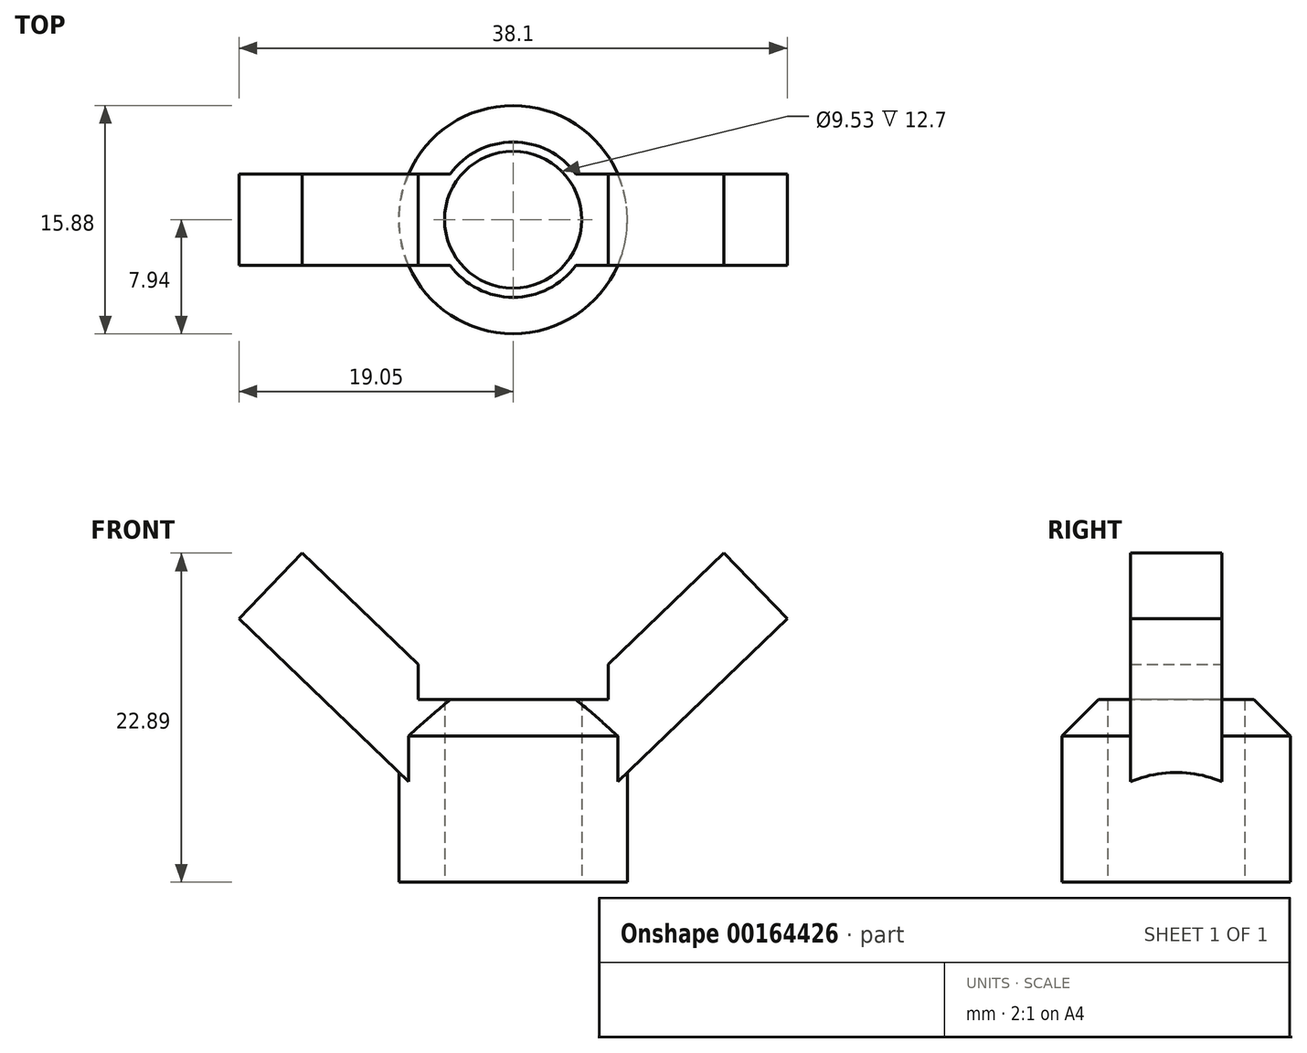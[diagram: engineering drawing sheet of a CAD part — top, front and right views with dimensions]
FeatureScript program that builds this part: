
annotation { "Feature Type Name" : "Feature", "Feature Type Description" : "" }
export const myFeature = defineFeature(function(context is Context, id is Id, definition is map)
    precondition{}
    {
        {
            var Q0;
            Q0=qCreatedBy(makeId("Front.planeOp"),FACE);
            var sketch = newSketch(context, id + "F0", { "sketchPlane" : qUnion([Q0])});
            skLineSegment(sketch, "E0", {"start": v(-6.6, 6.35) * mm, "end": v(-19.05, 18.32) * mm});
            skLineSegment(sketch, "E1", {"start": v(-19.05, 18.32) * mm, "end": v(-14.65, 22.9) * mm});
            skLineSegment(sketch, "E2", {"start": v(-14.65, 22.9) * mm, "end": v(-6.6, 15.16) * mm});
            skLineSegment(sketch, "E3", {"start": v(0, 0) * mm, "end": v(0, 75.67) * mm, "construction": true});
            skLineSegment(sketch, "E4", {"start": v(-6.6, 15.16) * mm, "end": v(-6.6, 6.35) * mm});
            skLineSegment(sketch, "E5", {"start": v(-6.6, 6.35) * mm, "end": v(-6.6, 0) * mm, "construction": true});
            skLineSegment(sketch, "E6", {"start": v(-6.6, 0) * mm, "end": v(0, 0) * mm, "construction": true});
            skLineSegment(sketch, "E7.MirrorCS", {"start": v(6.6, 6.35) * mm, "end": v(6.6, 0) * mm, "construction": true});
            skLineSegment(sketch, "E8.MirrorCS", {"start": v(6.6, 6.35) * mm, "end": v(19.05, 18.32) * mm});
            skLineSegment(sketch, "E9.MirrorCS", {"start": v(6.6, 15.16) * mm, "end": v(6.6, 6.35) * mm});
            skLineSegment(sketch, "E10.MirrorCS", {"start": v(14.65, 22.9) * mm, "end": v(6.6, 15.16) * mm});
            skLineSegment(sketch, "E11.MirrorCS", {"start": v(19.05, 18.32) * mm, "end": v(14.65, 22.9) * mm});
            skLineSegment(sketch, "E12.MirrorCS", {"start": v(6.6, 0) * mm, "end": v(0, 0) * mm, "construction": true});
            skSolve(sketch);
        }
        {
            var Q0;
            Q0=makeQuery(id+"F0.imprint","IMPRINT",FACE,{"disambiguationData":[TD([[makeQuery(id+"F0.imprint","IMPRINT",EDGE,{"derivedFrom":sQuery(id+"F0.wireOp",EDGE,"E0")}),-1.0]])]});
            var Q1;
            Q1=makeQuery(id+"F0.imprint","IMPRINT",FACE,{"disambiguationData":[TD([[makeQuery(id+"F0.imprint","IMPRINT",EDGE,{"derivedFrom":sQuery(id+"F0.wireOp",EDGE,"E8.MirrorCS")}),1.0]])]});
            extrude(context, id + "F1", {"entities" : qUnion([Q0, Q1]), "depth" : 3.17 * mm, "hasSecondDirection" : true, "secondDirectionOppositeDirection" : true, "secondDirectionDepth" : 3.17 * mm});
        }
        {
            var Q0;
            Q0=qCreatedBy(makeId("Top.planeOp"),FACE);
            var sketch = newSketch(context, id + "F2", { "sketchPlane" : qUnion([Q0])});
            skCircle(sketch, "E13", {"center": v(0, 0) * mm, "radius": 7.94 * mm});
            skCircle(sketch, "E14", {"center": v(0, 0) * mm, "radius": 4.76 * mm});
            skSolve(sketch);
        }
        {
            var Q0;
            Q0 = qSketchRegion(id + "F2", true);
            extrude(context, id + "F3", {"entities" : qUnion([Q0]), "operationType" : NewBodyOperationType.ADD, "depth" : 12.7 * mm});
        }
        {
            var Q0;
            {var subQ0=sQuery(id+"F2.wireOp",EDGE,"E13");Q0=makeQuery(id+"F3.boolean.opBoolean","SPLIT",EDGE,{"disambiguationData":[TD([makeQuery(id+"F1.opExtrude","CAP_FACE",FACE,{"disambiguationData":[OSD([sQuery(id+"F0.wireOp",EDGE,"E0"),sQuery(id+"F0.wireOp",EDGE,"E1"),sQuery(id+"F0.wireOp",EDGE,"E2"),sQuery(id+"F0.wireOp",EDGE,"E4")])],"isStart":false})])],"derivedFrom":makeQuery(id+"F3.opExtrude","CAP_EDGE",EDGE,{"disambiguationData":[OSD([subQ0])],"isStart":false})});}
            var Q1;
            {var subQ0=sQuery(id+"F2.wireOp",EDGE,"E13");Q1=makeQuery(id+"F3.boolean.opBoolean","SPLIT",EDGE,{"disambiguationData":[TD([makeQuery(id+"F1.opExtrude","CAP_FACE",FACE,{"disambiguationData":[OSD([sQuery(id+"F0.wireOp",EDGE,"E0"),sQuery(id+"F0.wireOp",EDGE,"E1"),sQuery(id+"F0.wireOp",EDGE,"E2"),sQuery(id+"F0.wireOp",EDGE,"E4")])],"isStart":true})])],"derivedFrom":makeQuery(id+"F3.opExtrude","CAP_EDGE",EDGE,{"disambiguationData":[OSD([subQ0])],"isStart":false})});}
            chamfer(context, id + "F4", {"entities" : qUnion([Q0, Q1]), "width" : 2.54 * mm, "tangentPropagation" : true});
        }
    });
